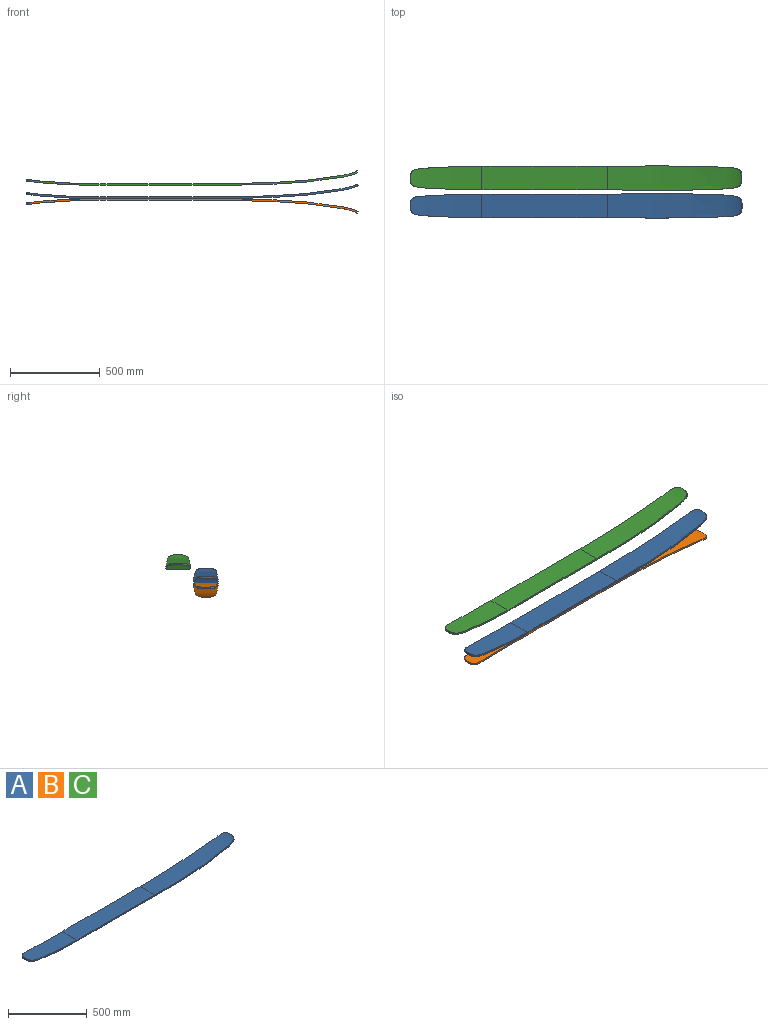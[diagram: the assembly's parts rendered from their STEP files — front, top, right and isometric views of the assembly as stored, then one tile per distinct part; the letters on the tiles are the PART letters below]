
ASSEMBLY  parts=3 mates=1
PART A: 26 faces, bbox 1850x136x80.8 mm
  f0: bspline ~39.32x34.05mm, area 556.2mm2, adj f1,f19,f20,f23
  f1: plane 20.72x9.85mm, normal (-0.98,0,0.17), area 207.2mm2, adj f0,f2,f20,f23
  f2: bspline ~39.32x34.05mm, area 556.2mm2, adj f1,f3,f20,f23
  f3: bspline ~39.64x14.64mm, area 390.3mm2, adj f2,f4,f20,f23
  f4: bspline ~328.41x25.05mm, area 3286.2mm2, adj f3,f5,f20,f23
  f5: extruded ~52.09x10mm, area 520.9mm2, adj f4,f6,f21,f24
  f6: cylinder r=61385.65mm len=649.96mm, axis (0,0,1), area 6499.6mm2, adj f5,f7,f21,f24
  f7: bspline ~257.54x15.32mm, area 2574.1mm2, adj f6,f8,f22,f25
  f8: bspline ~409.78x50.99mm, area 4111.1mm2, adj f7,f9,f22,f25
  f9: bspline ~51.53x22.16mm, area 510mm2, adj f8,f10,f22,f25
  f10: bspline ~39.18x34.97mm, area 558.2mm2, adj f9,f11,f22,f25
  f11: plane 29.43x8.77mm, normal (0.88,0,0.48), area 294.3mm2, adj f10,f12,f22,f25
  f12: bspline ~39.18x34.97mm, area 558.2mm2, adj f11,f13,f22,f25
  f13: bspline ~51.53x22.16mm, area 510mm2, adj f12,f14,f22,f25
  f14: bspline ~409.78x50.99mm, area 4111.1mm2, adj f13,f15,f22,f25
  f15: bspline ~257.54x15.32mm, area 2574.1mm2, adj f14,f16,f22,f25
  f16: cylinder r=61385.65mm len=649.96mm, axis (0,0,1), area 6499.6mm2, adj f15,f17,f21,f24
  f17: extruded ~52.09x10mm, area 520.9mm2, adj f16,f18,f21,f24
  f18: bspline ~328.41x25.05mm, area 3286.2mm2, adj f17,f19,f20,f23
  f19: bspline ~39.64x14.64mm, area 390.3mm2, adj f0,f18,f20,f23
  f20: extruded ~397.91x131.93mm, area 46752.3mm2, adj f0,f1,f2,f3,f4,f18,f19,f21
  f21: plane 702.04x132mm, normal (0,0,1), area 91741.3mm2, adj f5,f6,f16,f17,f20,f22
  f22: extruded ~743.51x136mm, area 96382.3mm2, adj f7,f8,f9,f10,f11,f12,f13,f14
  f23: extruded ~399.65x131.93mm, area 46922mm2, adj f0,f1,f2,f3,f4,f18,f19,f24
  f24: plane 702.04x132mm, normal (0,0,-1), area 91741.3mm2, adj f5,f6,f16,f17,f23,f25
  f25: extruded ~748.31x136mm, area 96888.3mm2, adj f7,f8,f9,f10,f11,f12,f13,f14
PART B: same geometry as A
PART C: same geometry as A
PLACE A t=(-195.65,-385.39,164.84)mm
PLACE B rot(axis=(1,0,0),180deg) t=(-195.65,-385.39,-15.16)mm
PLACE C t=(-195.68,-230.48,238.45)mm
MATE fastened B.f24 <-> A.f24  axis (0,0,1) through (-875.32,-385.39,74.84)mm
